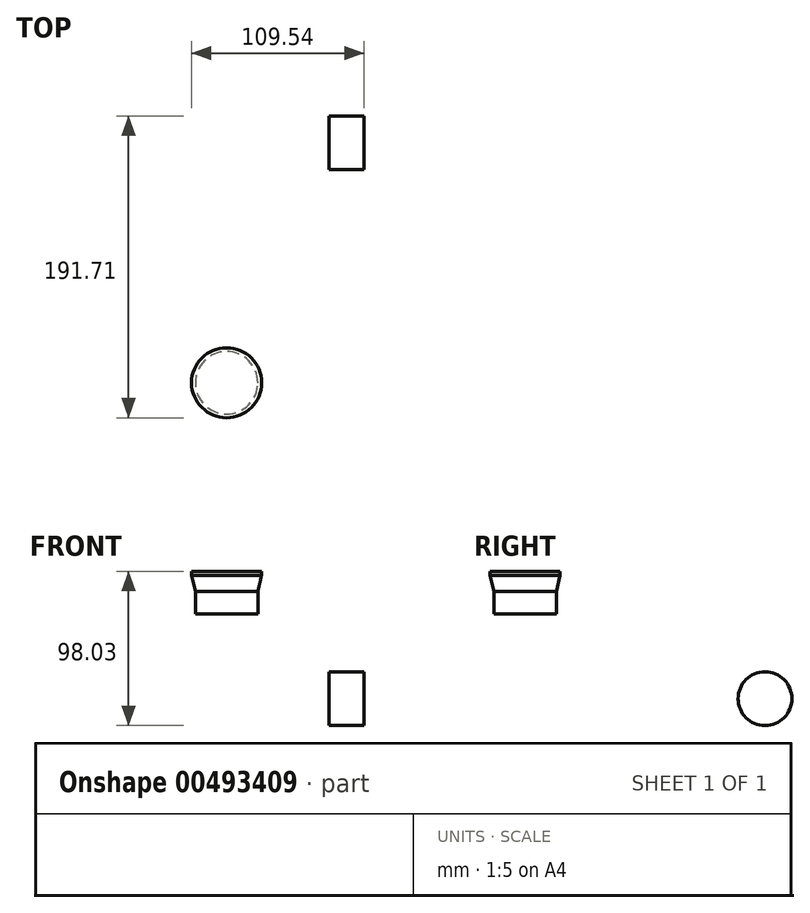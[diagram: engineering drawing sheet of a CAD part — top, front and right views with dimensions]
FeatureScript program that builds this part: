
annotation { "Feature Type Name" : "Feature", "Feature Type Description" : "" }
export const myFeature = defineFeature(function(context is Context, id is Id, definition is map)
    precondition{}
    {
        {
            assignVariable(context, id + "F0", {"name" : "deltay", "anyValue" : 61.1 * mm});
        }
        {
            var Q0;
            Q0=qCreatedBy(makeId("Top.planeOp"),FACE);
            cPlane(context, id + "F1", {"entities" : qUnion([Q0]), "cplaneType" : CPlaneType.OFFSET, "offset" : getVariable(context, 'deltay'), "width" : 152.4 * mm, "height" : 152.4 * mm});
        }
        {
            var Q0;
            Q0=qCreatedBy(id+"F1.planeOp",FACE);
            var sketch = newSketch(context, id + "F2", { "sketchPlane" : qUnion([Q0])});
            skCircle(sketch, "E0", {"center": v(-76.2, 0) * mm, "radius": 19.85 * mm});
            skSolve(sketch);
        }
        {
            var Q0;
            Q0=qSketchRegion(id+"F2",true);
            extrude(context, id + "F3", {"entities" : qUnion([Q0]), "oppositeDirection" : true, "depth" : 7.14 * mm, "hasSecondDirection" : true, "secondDirectionOppositeDirection" : false, "secondDirectionDepth" : 7.14 * mm});
        }
        {
            var Q0;
            Q0=makeQuery(id+"F3.opExtrude","CAP_FACE",FACE,{"disambiguationData":[OSD([sQuery(id+"F2.wireOp",EDGE,"E0")])],"isStart":true});
            cPlane(context, id + "F4", {"entities" : qUnion([Q0]), "cplaneType" : CPlaneType.OFFSET, "offset" : 12.7 * mm, "width" : 152.4 * mm, "height" : 152.4 * mm});
        }
        {
            var Q0;
            Q0=qCreatedBy(id+"F4.planeOp",FACE);
            var sketch = newSketch(context, id + "F5", { "sketchPlane" : qUnion([Q0])});
            skCircle(sketch, "E1", {"center": v(-76.2, 0) * mm, "radius": 22.22 * mm});
            skSolve(sketch);
        }
        {
            var Q0;
            Q0=qSketchRegion(id+"F5",true);
            extrude(context, id + "F6", {"entities" : qUnion([Q0]), "oppositeDirection" : true, "depth" : 2.54 * mm});
        }
        {
            var Q0;
            Q0=makeQuery(id+"F3.opExtrude","CAP_FACE",FACE,{"disambiguationData":[OSD([sQuery(id+"F2.wireOp",EDGE,"E0")])],"isStart":true});
            var Q1;
            Q1=makeQuery(id+"F6.opExtrude","CAP_FACE",FACE,{"disambiguationData":[OSD([sQuery(id+"F5.wireOp",EDGE,"E1")])],"isStart":false});
            loft(context, id + "F7", {"sheetProfilesArray" : [{ "sheetProfileEntities" : qUnion([Q0]) }, { "sheetProfileEntities" : qUnion([Q1]) }]});
        }
        {
            var Q0;
            Q0=qCreatedBy(makeId("Right.planeOp"),FACE);
            var sketch = newSketch(context, id + "F8", { "sketchPlane" : qUnion([Q0])});
            skCircle(sketch, "E2", {"center": v(152.4, 0) * mm, "radius": 17.08 * mm});
            skLineSegment(sketch, "E3", {"start": v(152.4, 0) * mm, "end": v(169.48, 0) * mm, "construction": true});
            skSolve(sketch);
        }
        {
            var Q0;
            Q0=qSketchRegion(id+"F8",true);
            extrude(context, id + "F9", {"entities" : qUnion([Q0]), "depth" : 11.1 * mm, "hasSecondDirection" : true, "secondDirectionOppositeDirection" : true, "secondDirectionDepth" : 11.1 * mm});
        }
        {
            var Q0;
            Q0=sQuery(id+"F5.wireOp",VERTEX,"E1.center");
            var Q1;
            Q1=sQuery(id+"F2.wireOp",VERTEX,"E0.center");
            var Q2;
            Q2=sQuery(id+"F8.wireOp",VERTEX,"E2.center");
            cPlane(context, id + "F10", {"entities" : qUnion([Q0, Q1, Q2]), "cplaneType" : CPlaneType.THREE_POINT, "offset" : 25.4 * mm, "width" : 152.4 * mm, "height" : 152.4 * mm});
        }
        {
            var Q0;
            Q0=qCreatedBy(id+"F10.planeOp",FACE);
            var sketch = newSketch(context, id + "F11", { "sketchPlane" : qUnion([Q0])});
            skLineSegment(sketch, "E4", {"start": v(15.03, 61.11) * mm, "end": v(-136.31, 0) * mm, "construction": true});
            skLineSegment(sketch, "E5", {"start": v(15.03, 61.11) * mm, "end": v(53.13, 61.11) * mm, "construction": true});
            skSolve(sketch);
        }
        {
            var Q0;
            Q0=makeQuery(id+"F9.opExtrude","CAP_FACE",FACE,{"disambiguationData":[OSD([sQuery(id+"F8.wireOp",EDGE,"E2")])],"isStart":true});
            var sketch = newSketch(context, id + "F12", { "sketchPlane" : qUnion([Q0])});
            skPoint(sketch, "E6", {"position": v(-152.4, 0) * mm});
            skSolve(sketch);
        }
        {
            var Q0;
            Q0=sQuery(id+"F11.wireOp",VERTEX,"E4.end");
            var Q1;
            Q1=sQuery(id+"F12.wireOp",VERTEX,"E6");
            var Q2;
            Q2=sQuery(id+"F11.wireOp",VERTEX,"E5.start");
            cPlane(context, id + "F13", {"entities" : qUnion([Q0, Q1, Q2]), "cplaneType" : CPlaneType.THREE_POINT, "offset" : 25.4 * mm, "width" : 152.4 * mm, "height" : 152.4 * mm});
        }
        {
            var Q0;
            Q0=qCreatedBy(id+"F1.planeOp",FACE);
            var sketch = newSketch(context, id + "F14", { "sketchPlane" : qUnion([Q0])});
            skLineSegment(sketch, "E7", {"start": v(-76.2, 0) * mm, "end": v(0, 30.69) * mm, "construction": true});
            skPoint(sketch, "E8", {"position": v(-57.79, 7.42) * mm});
            skSolve(sketch);
        }
        {
            var Q0;
            Q0=makeQuery(id+"F3.opExtrude","CAP_FACE",FACE,{"disambiguationData":[OSD([sQuery(id+"F2.wireOp",EDGE,"E0")])],"isStart":false});
            var sketch = newSketch(context, id + "F15", { "sketchPlane" : qUnion([Q0])});
            skPoint(sketch, "E9", {"position": v(-76.2, 0) * mm});
            skSolve(sketch);
        }
        {
            var Q0;
            Q0=sQuery(id+"F14.wireOp",EDGE,"E7");
            var Q1;
            Q1=sQuery(id+"F15.wireOp",VERTEX,"E9");
            cPlane(context, id + "F16", {"entities" : qUnion([Q0, Q1]), "cplaneType" : CPlaneType.LINE_ANGLE, "offset" : 25.4 * mm, "angle" : 0 * degree, "width" : 152.4 * mm, "height" : 152.4 * mm});
        }
        {
            var Q0;
            Q0=qCreatedBy(makeId("Right.planeOp"),FACE);
            var sketch = newSketch(context, id + "F17", { "sketchPlane" : qUnion([Q0])});
            skLineSegment(sketch, "E10", {"start": v(152.4, 0) * mm, "end": v(7.55, 61.11) * mm, "construction": true});
            skPoint(sketch, "E11", {"position": v(136.66, 6.64) * mm});
            skSolve(sketch);
        }
        {
            var Q0;
            Q0=makeQuery(id+"F9.opExtrude","CAP_FACE",FACE,{"disambiguationData":[OSD([sQuery(id+"F8.wireOp",EDGE,"E2")])],"isStart":true});
            var sketch = newSketch(context, id + "F18", { "sketchPlane" : qUnion([Q0])});
            skPoint(sketch, "E12", {"position": v(-152.4, 0) * mm});
            skSolve(sketch);
        }
        {
            var Q0;
            Q0=sQuery(id+"F15.wireOp",VERTEX,"E9");
            var Q1;
            Q1=sQuery(id+"F14.wireOp",VERTEX,"E7.start");
            var Q2;
            Q2=sQuery(id+"F8.wireOp",VERTEX,"E2.center");
            cPlane(context, id + "F19", {"entities" : qUnion([Q0, Q1, Q2]), "cplaneType" : CPlaneType.THREE_POINT, "offset" : 25.4 * mm, "width" : 152.4 * mm, "height" : 152.4 * mm});
        }
    });
